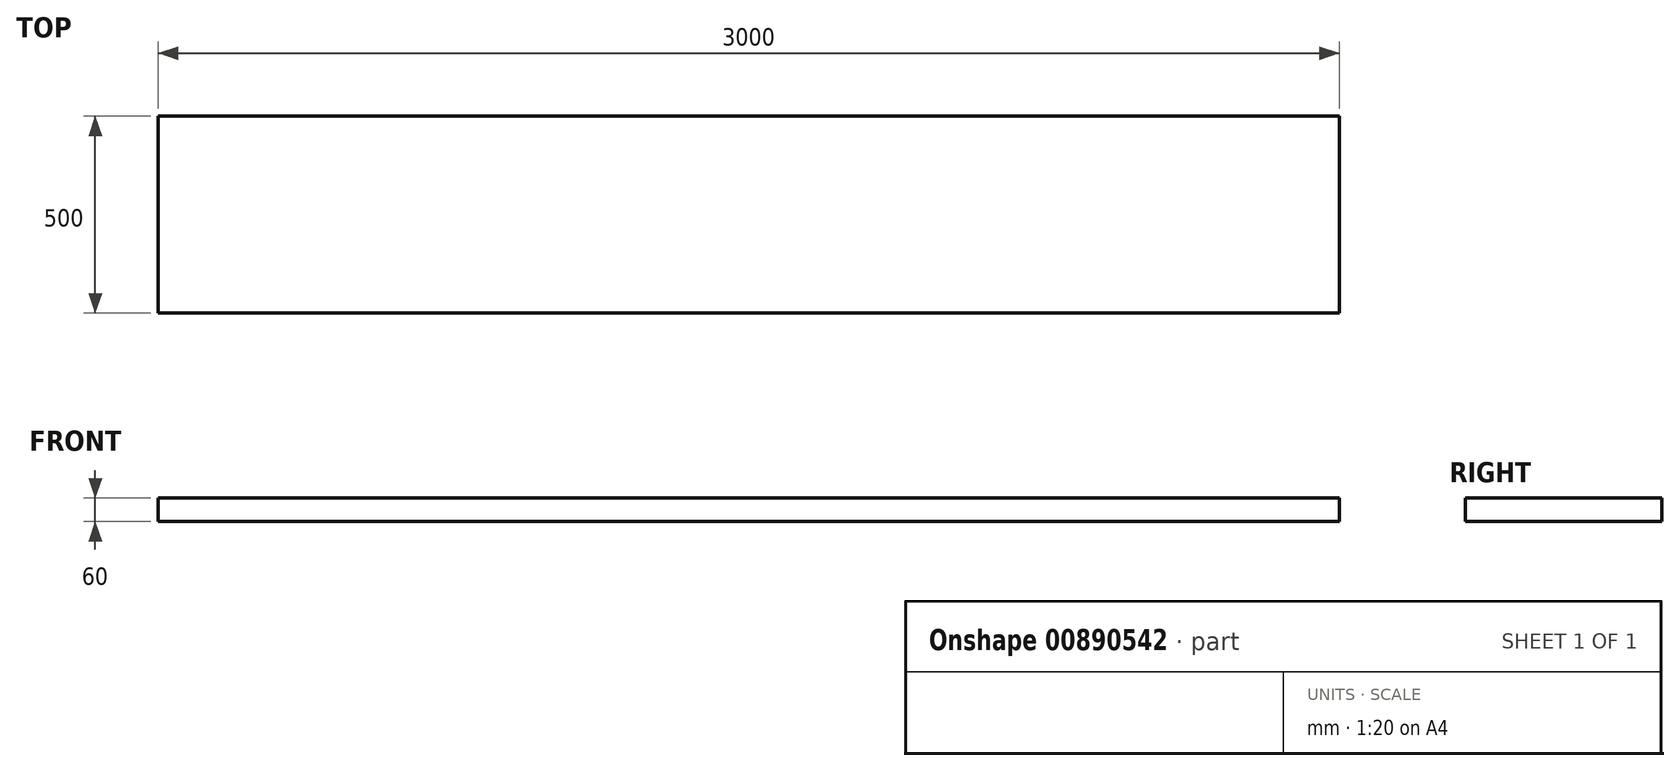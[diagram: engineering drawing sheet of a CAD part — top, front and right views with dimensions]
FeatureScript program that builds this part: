
annotation { "Feature Type Name" : "Feature", "Feature Type Description" : "" }
export const myFeature = defineFeature(function(context is Context, id is Id, definition is map)
    precondition{}
    {
        {
            var Q0;
            Q0=qCreatedBy(makeId("Top.planeOp"),FACE);
            var sketch = newSketch(context, id + "F0", { "sketchPlane" : qUnion([Q0])});
            skLineSegment(sketch, "E0.bottom", {"start": v(1500, 250) * mm, "end": v(-1500, 250) * mm});
            skLineSegment(sketch, "E0.top", {"start": v(1500, -250) * mm, "end": v(-1500, -250) * mm});
            skLineSegment(sketch, "E0.left", {"start": v(1500, 250) * mm, "end": v(1500, -250) * mm});
            skLineSegment(sketch, "E0.right", {"start": v(-1500, 250) * mm, "end": v(-1500, -250) * mm});
            skPoint(sketch, "E0.middle", {"position": v(0, 0) * mm});
            skSolve(sketch);
        }
        {
            var Q0;
            Q0=makeQuery(id+"F0.imprint","IMPRINT",FACE,{"disambiguationData":[TD([[makeQuery(id+"F0.imprint","IMPRINT",EDGE,{"derivedFrom":sQuery(id+"F0.wireOp",EDGE,"E0.bottom")}),1.0]])]});
            extrude(context, id + "F1", {"entities" : qUnion([Q0]), "depth" : 60 * mm, "offsetDistance" : 25 * mm});
        }
    });
